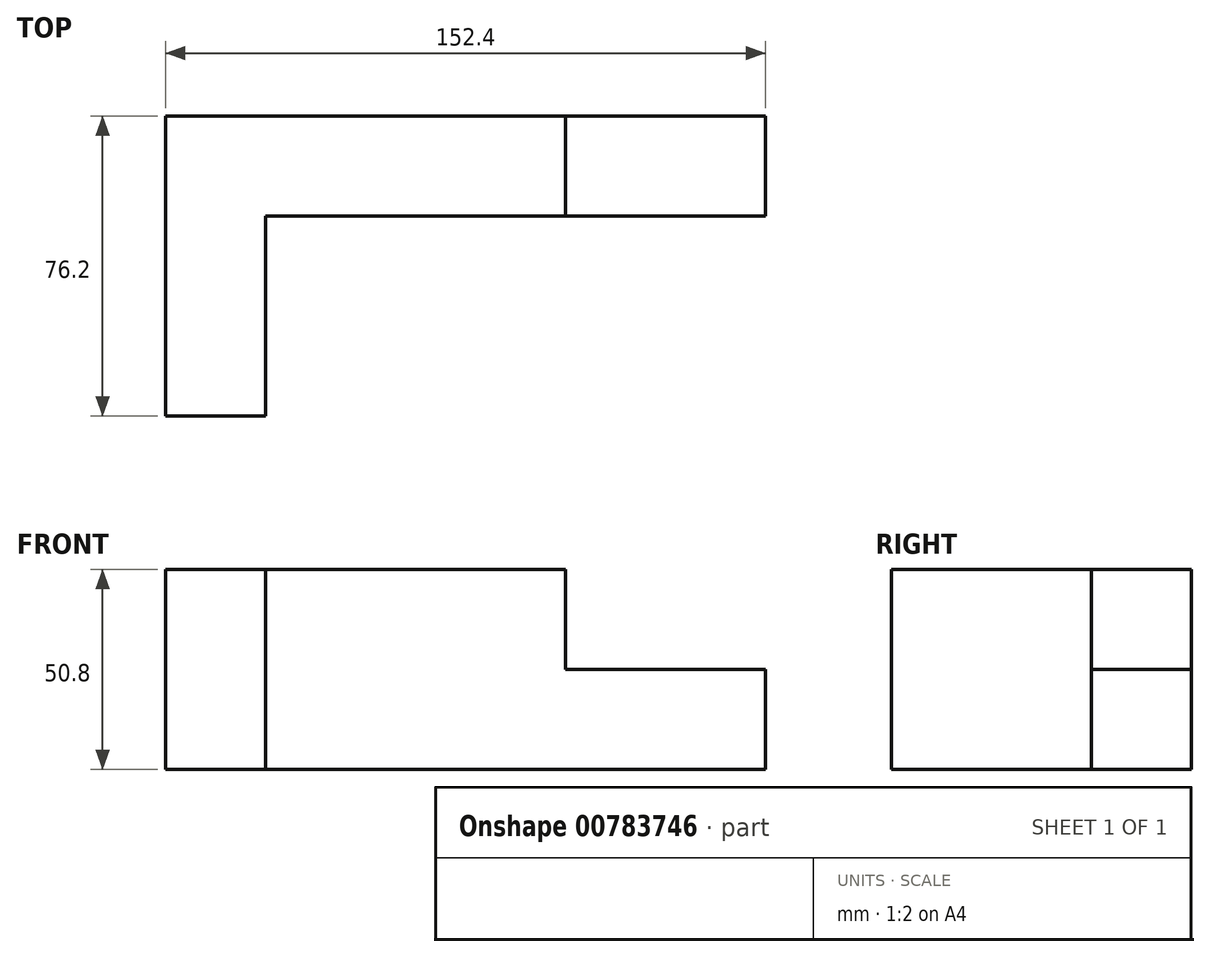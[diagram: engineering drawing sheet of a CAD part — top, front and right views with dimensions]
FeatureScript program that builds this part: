
annotation { "Feature Type Name" : "Feature", "Feature Type Description" : "" }
export const myFeature = defineFeature(function(context is Context, id is Id, definition is map)
    precondition{}
    {
        {
            var Q0;
            Q0=qCreatedBy(makeId("Front.planeOp"),FACE);
            var sketch = newSketch(context, id + "F0", { "sketchPlane" : qUnion([Q0])});
            skLineSegment(sketch, "E0", {"start": v(0, 0) * mm, "end": v(152.4, 0) * mm});
            skLineSegment(sketch, "E1", {"start": v(0, 0) * mm, "end": v(0, 50.8) * mm});
            skLineSegment(sketch, "E2", {"start": v(0, 50.8) * mm, "end": v(152.4, 50.8) * mm});
            skLineSegment(sketch, "E3", {"start": v(152.4, 50.8) * mm, "end": v(152.4, 0) * mm});
            skSolve(sketch);
        }
        {
            var Q0;
            Q0=makeQuery(id+"F0.imprint","IMPRINT",FACE,{"disambiguationData":[TD([[makeQuery(id+"F0.imprint","IMPRINT",EDGE,{"derivedFrom":sQuery(id+"F0.wireOp",EDGE,"E0")}),1.0]])]});
            extrude(context, id + "F1", {"entities" : qUnion([Q0]), "depth" : 25.4 * mm, "offsetDistance" : 25.4 * mm});
        }
        {
            var Q0;
            Q0=makeQuery(id+"F1.opExtrude","CAP_FACE",FACE,{"disambiguationData":[OSD([sQuery(id+"F0.wireOp",EDGE,"E0"),sQuery(id+"F0.wireOp",EDGE,"E1"),sQuery(id+"F0.wireOp",EDGE,"E2"),sQuery(id+"F0.wireOp",EDGE,"E3")])],"isStart":false});
            var sketch = newSketch(context, id + "F2", { "sketchPlane" : qUnion([Q0])});
            skLineSegment(sketch, "E4", {"start": v(0, 50.8) * mm, "end": v(25.4, 50.8) * mm});
            skLineSegment(sketch, "E5", {"start": v(25.4, 50.8) * mm, "end": v(25.4, 0) * mm});
            skLineSegment(sketch, "E6", {"start": v(0, 50.8) * mm, "end": v(0, 0) * mm});
            skLineSegment(sketch, "E7", {"start": v(25.4, 0) * mm, "end": v(0, 0) * mm});
            skSolve(sketch);
        }
        {
            var Q0;
            Q0=makeQuery(id+"F2.imprint","IMPRINT",FACE,{"disambiguationData":[TD([[makeQuery(id+"F2.imprint","IMPRINT",EDGE,{"derivedFrom":sQuery(id+"F2.wireOp",EDGE,"E4")}),-1.0]])]});
            extrude(context, id + "F3", {"entities" : qUnion([Q0]), "operationType" : NewBodyOperationType.ADD, "depth" : 50.8 * mm, "offsetDistance" : 25.4 * mm});
        }
        {
            var Q0;
            Q0=makeQuery(id+"F1.opExtrude","SWEPT_FACE",FACE,{"disambiguationData":[OSD([sQuery(id+"F0.wireOp",EDGE,"E3")])]});
            var sketch = newSketch(context, id + "F4", { "sketchPlane" : qUnion([Q0])});
            skLineSegment(sketch, "E8", {"start": v(-25.4, 0) * mm, "end": v(-25.4, 25.4) * mm});
            skLineSegment(sketch, "E9", {"start": v(-25.4, 25.4) * mm, "end": v(0, 25.4) * mm});
            skLineSegment(sketch, "E10", {"start": v(0, 25.4) * mm, "end": v(0, 0) * mm});
            skLineSegment(sketch, "E11", {"start": v(0, 0) * mm, "end": v(-25.4, 0) * mm});
            skSolve(sketch);
        }
        {
            var Q0;
            {var subQ0=sQuery(id+"F4.wireOp",EDGE,"E9");Q0=makeQuery(id+"F4.imprint","IMPRINT",FACE,{"disambiguationData":[TD([[makeQuery(id+"F4.imprint","IMPRINT",EDGE,{"derivedFrom":subQ0}),1.0]])]});}
            extrude(context, id + "F5", {"entities" : qUnion([Q0]), "operationType" : NewBodyOperationType.REMOVE, "oppositeDirection" : true, "depth" : 50.8 * mm, "offsetDistance" : 25.4 * mm});
        }
    });
